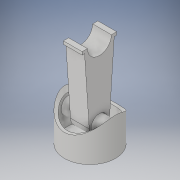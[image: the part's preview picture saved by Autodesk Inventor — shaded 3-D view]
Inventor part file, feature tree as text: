
AUTODESK INVENTOR PART (.ipt)
format: ipt  version: 2018 (Build 220112000, 112)  size: 183,296 bytes
history: native  units: in
note: dims shown in document units (in); Inventor stores cm internally (conversion verified against a paired STEP export)
features: extrude x7, sketch x7, plane x2, mirror x1
ambient origin geometry x8: Origin, YZ Plane, XZ Plane, XY Plane, X Axis, Y Axis, Z Axis, Center Point
bodies: Solid1 (feature_tree)
feature tree (17):
  extrude  "Extrusion1"  Depth=2.5in TaperAngle=0.0deg
  extrude  "Extrusion2"  Depth=1.5in TaperAngle=0.0deg
  plane  "Work Plane1"
  extrude  "Extrusion3"  Depth=3.0in
  extrude  "Extrusion4"  Depth=1.0in
  extrude  "Extrusion5"  TaperAngle=0.0deg  [1 undecoded]
  extrude  "Extrusion6"  Depth=1.1in
  plane  "Work Plane2"
  extrude  "Extrusion7"  Depth=1.5in
  mirror  "Mirror1"
  sketch  "Sketch1"  dims[d0=3.4in d1=2.5in d2=0.0in]
  sketch  "Sketch2"  dims[d4=1.5in d5=4.0in d6=0.0in]
  sketch  "Sketch3"  dims[d7=-2.5in d8=3.0in]
  sketch  "Sketch4"  dims[d9=2.25in d10=0.0in d11=1.0in]
  sketch  "Sketch5"  dims[d12=1.0in d13=0.0in]
  sketch  "Sketch6"  dims[d14=3.1in d15=0.0in d16=1.1in]
  sketch  "Sketch7"  dims[d17=1.35in d18=1.5in d19=1.7in d20=1.6in d21=0.0in d22=4.7in d23=2.0in d24=1.25in d25=0.0in d26=100.0in d27=0.0in d28=-0.9in d29=0.2in d30=0.25in d31=0.0in]
note: 1 required parameter value undecoded (feature->parameter linkage not recoverable at this tier; creation-order binding heuristic only, values carry confidence <= 0.55)
